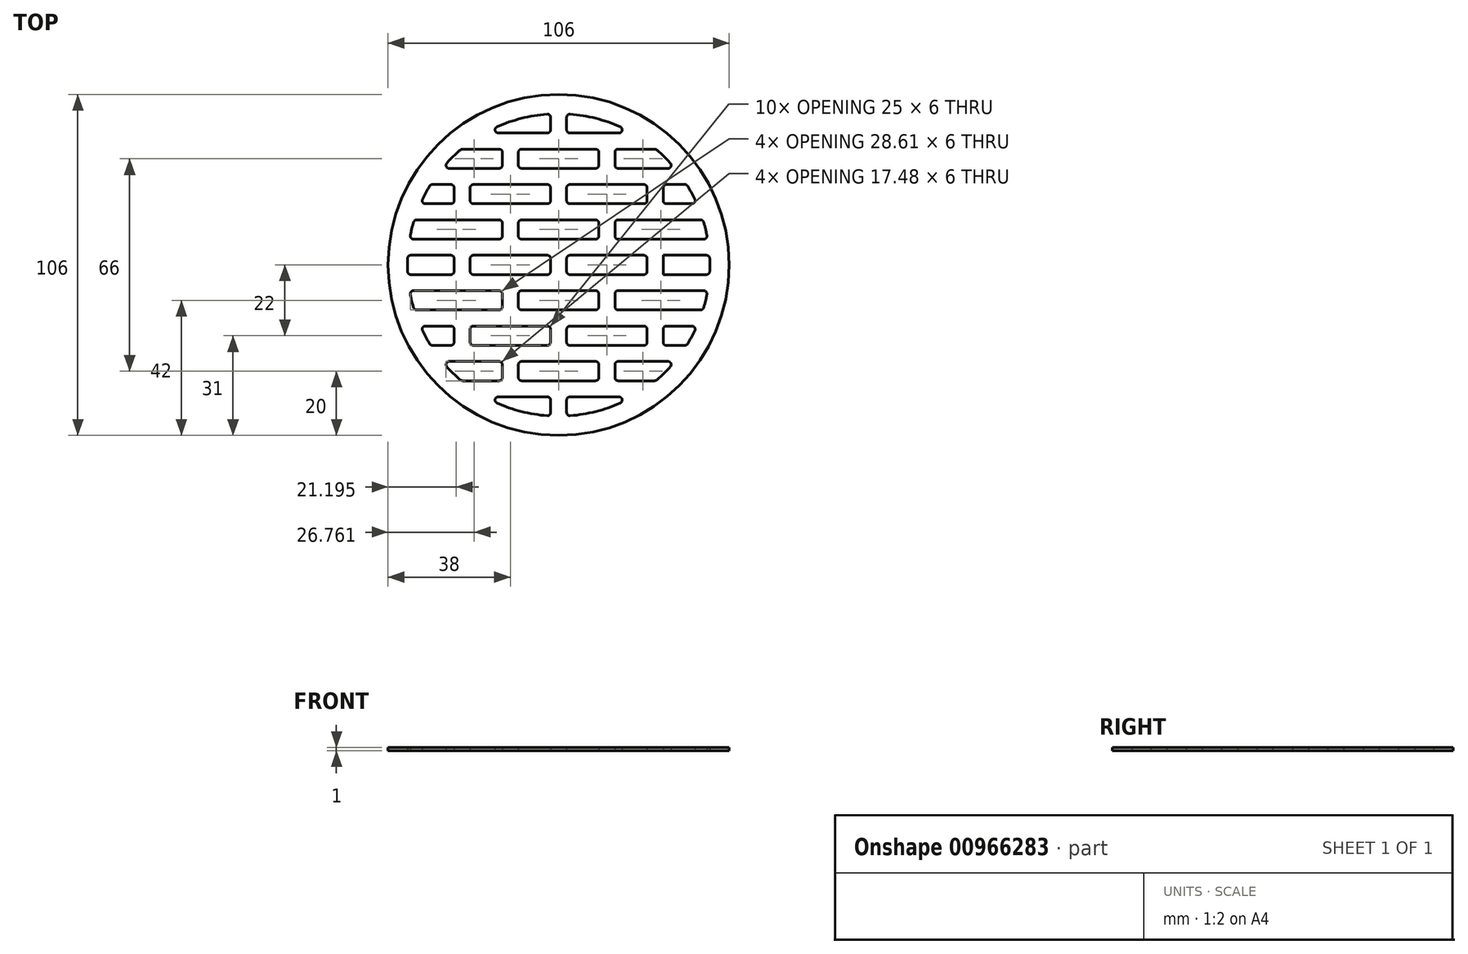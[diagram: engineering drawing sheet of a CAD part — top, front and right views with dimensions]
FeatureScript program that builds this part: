
annotation { "Feature Type Name" : "Feature", "Feature Type Description" : "" }
export const myFeature = defineFeature(function(context is Context, id is Id, definition is map)
    precondition{}
    {
        {
            var Q0;
            Q0=qCreatedBy(makeId("Top.planeOp"),FACE);
            var sketch = newSketch(context, id + "F0", { "sketchPlane" : qUnion([Q0])});
            skCircle(sketch, "E0", {"center": v(0, 0) * mm, "radius": 53 * mm});
            skArc(sketch, "E1", {"start": v(22.98, 41) * mm, "mid": v(13.08, 45.14) * mm, "end": v(2.5, 46.93) * mm});
            skLineSegment(sketch, "E2", {"start": v(-47, 0) * mm, "end": v(47, 0) * mm, "construction": true});
            skLineSegment(sketch, "E3.0", {"start": v(-46.9, -3) * mm, "end": v(-32.5, -3) * mm});
            skLineSegment(sketch, "E4.0", {"start": v(-46.9, 3) * mm, "end": v(-32.5, 3) * mm});
            skLineSegment(sketch, "E5", {"start": v(0, 47) * mm, "end": v(0, -47) * mm, "construction": true});
            skLineSegment(sketch, "E6.0", {"start": v(2.5, 46.93) * mm, "end": v(2.5, 41) * mm});
            skLineSegment(sketch, "E7.0", {"start": v(-2.5, 46.93) * mm, "end": v(-2.5, 41) * mm});
            skLineSegment(sketch, "E8.0.1.0", {"start": v(-46.9, 8) * mm, "end": v(-17.5, 8) * mm});
            skLineSegment(sketch, "E8.0.1.1", {"start": v(-44.87, 14) * mm, "end": v(-17.5, 14) * mm});
            skLineSegment(sketch, "E8.0.2.0", {"start": v(-42.99, 19) * mm, "end": v(-32.5, 19) * mm});
            skLineSegment(sketch, "E8.0.2.1", {"start": v(-39.8, 25) * mm, "end": v(-32.5, 25) * mm});
            skLineSegment(sketch, "E8.0.3.0", {"start": v(-36.18, 30) * mm, "end": v(-17.5, 30) * mm});
            skLineSegment(sketch, "E8.direction1", {"start": v(-46.9, -3) * mm, "end": v(-32.5, -3) * mm, "construction": true});
            skLineSegment(sketch, "E8.direction2", {"start": v(-46.9, -3) * mm, "end": v(-46.9, 8) * mm, "construction": true});
            skLineSegment(sketch, "E9.trimOffspring", {"start": v(-27.5, 3) * mm, "end": v(-27.5, -3) * mm});
            skLineSegment(sketch, "E10.trimOffspring", {"start": v(-32.5, 3) * mm, "end": v(-32.5, -3) * mm});
            skLineSegment(sketch, "E11.trimOffspring", {"start": v(-2.5, 3) * mm, "end": v(-2.5, -3) * mm});
            skLineSegment(sketch, "E12.trimOffspring", {"start": v(2.5, 3) * mm, "end": v(2.5, -3) * mm});
            skLineSegment(sketch, "E13.trimOffspring", {"start": v(-12.5, 14) * mm, "end": v(-12.5, 8) * mm});
            skLineSegment(sketch, "E14.trimOffspring", {"start": v(-17.5, 14) * mm, "end": v(-17.5, 8) * mm});
            skLineSegment(sketch, "E15.trimOffspring", {"start": v(2.5, 25) * mm, "end": v(2.5, 19) * mm});
            skLineSegment(sketch, "E16.trimOffspring", {"start": v(-2.5, 25) * mm, "end": v(-2.5, 19) * mm});
            skLineSegment(sketch, "E17.trimOffspring", {"start": v(-27.5, 25) * mm, "end": v(-27.5, 19) * mm});
            skLineSegment(sketch, "E18.trimOffspring", {"start": v(-32.5, 25) * mm, "end": v(-32.5, 19) * mm});
            skLineSegment(sketch, "E19.trimOffspring", {"start": v(-12.5, 36) * mm, "end": v(-12.5, 30) * mm});
            skLineSegment(sketch, "E20.trimOffspring", {"start": v(-17.5, 36) * mm, "end": v(-17.5, 30) * mm});
            skLineSegment(sketch, "E21.trimOffspring", {"start": v(-22.98, 41) * mm, "end": v(-2.5, 41) * mm});
            skLineSegment(sketch, "E22.trimOffspring", {"start": v(-30.22, 36) * mm, "end": v(-17.5, 36) * mm});
            skPoint(sketch, "E23.orphan", {"position": v(-46.9, 30) * mm});
            skPoint(sketch, "E24.orphan", {"position": v(-46.9, 25) * mm});
            skPoint(sketch, "E25.orphan", {"position": v(-46.9, 19) * mm});
            skPoint(sketch, "E26.orphan", {"position": v(-46.9, 14) * mm});
            skPoint(sketch, "E27.orphan", {"position": v(46.9, 8) * mm});
            skPoint(sketch, "E28.orphan", {"position": v(46.9, 14) * mm});
            skPoint(sketch, "E29.orphan", {"position": v(46.9, 19) * mm});
            skPoint(sketch, "E30.orphan", {"position": v(46.9, 25) * mm});
            skPoint(sketch, "E31.orphan", {"position": v(46.9, 30) * mm});
            skPoint(sketch, "E32.orphan", {"position": v(46.9, 41) * mm});
            skArc(sketch, "E33.trimOffspring", {"start": v(-30.22, 36) * mm, "mid": v(-33.33, 33.13) * mm, "end": v(-36.18, 30) * mm});
            skArc(sketch, "E34.trimOffspring", {"start": v(-39.8, 25) * mm, "mid": v(-41.5, 22.06) * mm, "end": v(-42.99, 19) * mm});
            skArc(sketch, "E35.trimOffspring", {"start": v(36.18, 30) * mm, "mid": v(33.33, 33.13) * mm, "end": v(30.22, 36) * mm});
            skArc(sketch, "E36.trimOffspring", {"start": v(42.99, 19) * mm, "mid": v(41.5, 22.06) * mm, "end": v(39.8, 25) * mm});
            skArc(sketch, "E37.trimOffspring", {"start": v(-44.87, 14) * mm, "mid": v(-45.69, 11.02) * mm, "end": v(-46.31, 8) * mm});
            skArc(sketch, "E38.trimOffspring", {"start": v(46.31, 8) * mm, "mid": v(45.69, 11.02) * mm, "end": v(44.87, 14) * mm});
            skArc(sketch, "E39.trimOffspring", {"start": v(-46.9, 3) * mm, "mid": v(-47, 0) * mm, "end": v(-46.9, -3) * mm});
            skLineSegment(sketch, "E40.MirrorCS", {"start": v(27.5, 3) * mm, "end": v(27.5, -3) * mm});
            skLineSegment(sketch, "E41.MirrorCS", {"start": v(32.5, 3) * mm, "end": v(32.5, -3) * mm});
            skLineSegment(sketch, "E42.MirrorCS", {"start": v(17.5, 14) * mm, "end": v(17.5, 8) * mm});
            skLineSegment(sketch, "E43.MirrorCS", {"start": v(12.5, 14) * mm, "end": v(12.5, 8) * mm});
            skLineSegment(sketch, "E44.MirrorCS", {"start": v(27.5, 25) * mm, "end": v(27.5, 19) * mm});
            skLineSegment(sketch, "E45.MirrorCS", {"start": v(32.5, 25) * mm, "end": v(32.5, 19) * mm});
            skLineSegment(sketch, "E46.MirrorCS", {"start": v(12.5, 36) * mm, "end": v(12.5, 30) * mm});
            skLineSegment(sketch, "E47.MirrorCS", {"start": v(17.5, 36) * mm, "end": v(17.5, 30) * mm});
            skLineSegment(sketch, "E48.MirrorCS", {"start": v(-12.5, -36) * mm, "end": v(-12.5, -30) * mm});
            skLineSegment(sketch, "E49.MirrorCS", {"start": v(12.5, -36) * mm, "end": v(12.5, -30) * mm});
            skArc(sketch, "E50.MirrorCS", {"start": v(46.31, -8) * mm, "mid": v(45.69, -11.02) * mm, "end": v(44.87, -14) * mm});
            skArc(sketch, "E51.MirrorCS", {"start": v(-44.87, -14) * mm, "mid": v(-45.69, -11.02) * mm, "end": v(-46.31, -8) * mm});
            skLineSegment(sketch, "E52.MirrorCS", {"start": v(-17.5, -36) * mm, "end": v(-17.5, -30) * mm});
            skLineSegment(sketch, "E53.MirrorCS", {"start": v(17.5, -36) * mm, "end": v(17.5, -30) * mm});
            skLineSegment(sketch, "E54.MirrorCS", {"start": v(-12.5, -14) * mm, "end": v(-12.5, -8) * mm});
            skPoint(sketch, "E55.MirrorP", {"position": v(-46.9, -25) * mm});
            skLineSegment(sketch, "E56.MirrorCS", {"start": v(2.5, -46.93) * mm, "end": v(2.5, -41) * mm});
            skLineSegment(sketch, "E57.MirrorCS", {"start": v(2.5, -25) * mm, "end": v(2.5, -19) * mm});
            skArc(sketch, "E58.MirrorCS", {"start": v(-30.22, -36) * mm, "mid": v(-33.33, -33.13) * mm, "end": v(-36.18, -30) * mm});
            skLineSegment(sketch, "E59.MirrorCS", {"start": v(12.5, -14) * mm, "end": v(12.5, -8) * mm});
            skArc(sketch, "E60.MirrorCS", {"start": v(42.99, -19) * mm, "mid": v(41.5, -22.06) * mm, "end": v(39.8, -25) * mm});
            skPoint(sketch, "E61.MirrorP", {"position": v(46.9, -14) * mm});
            skArc(sketch, "E62.MirrorCS", {"start": v(22.98, -41) * mm, "mid": v(13.08, -45.14) * mm, "end": v(2.5, -46.93) * mm});
            skLineSegment(sketch, "E63.MirrorCS", {"start": v(-44.87, -14) * mm, "end": v(-17.5, -14) * mm});
            skLineSegment(sketch, "E64.MirrorCS", {"start": v(-2.5, -25) * mm, "end": v(-2.5, -19) * mm});
            skLineSegment(sketch, "E65.MirrorCS", {"start": v(32.5, -25) * mm, "end": v(32.5, -19) * mm});
            skLineSegment(sketch, "E66.MirrorCS", {"start": v(17.5, -14) * mm, "end": v(17.5, -8) * mm});
            skPoint(sketch, "E67.MirrorP", {"position": v(-46.9, -30) * mm});
            skLineSegment(sketch, "E68.MirrorCS", {"start": v(-17.5, -14) * mm, "end": v(-17.5, -8) * mm});
            skArc(sketch, "E69.MirrorCS", {"start": v(36.18, -30) * mm, "mid": v(33.33, -33.13) * mm, "end": v(30.22, -36) * mm});
            skPoint(sketch, "E70.MirrorP", {"position": v(-46.9, -19) * mm});
            skLineSegment(sketch, "E71.MirrorCS", {"start": v(-2.5, -46.93) * mm, "end": v(-2.5, -41) * mm});
            skPoint(sketch, "E72.MirrorP", {"position": v(46.9, -41) * mm});
            skPoint(sketch, "E73.MirrorP", {"position": v(46.9, -8) * mm});
            skLineSegment(sketch, "E74.MirrorCS", {"start": v(-46.31, -8) * mm, "end": v(-17.5, -8) * mm});
            skArc(sketch, "E75.MirrorCS", {"start": v(-39.8, -25) * mm, "mid": v(-41.5, -22.06) * mm, "end": v(-42.99, -19) * mm});
            skLineSegment(sketch, "E76.MirrorCS", {"start": v(-32.5, -25) * mm, "end": v(-32.5, -19) * mm});
            skLineSegment(sketch, "E77.MirrorCS", {"start": v(-36.18, -30) * mm, "end": v(-17.5, -30) * mm});
            skPoint(sketch, "E78.MirrorP", {"position": v(-46.9, -14) * mm});
            skLineSegment(sketch, "E79.MirrorCS", {"start": v(-30.22, -36) * mm, "end": v(-17.5, -36) * mm});
            skPoint(sketch, "E80.MirrorP", {"position": v(46.9, -30) * mm});
            skLineSegment(sketch, "E81.MirrorCS", {"start": v(-22.98, -41) * mm, "end": v(-2.5, -41) * mm});
            skLineSegment(sketch, "E82.MirrorCS", {"start": v(-27.5, -25) * mm, "end": v(-27.5, -19) * mm});
            skPoint(sketch, "E83.MirrorP", {"position": v(46.9, -25) * mm});
            skLineSegment(sketch, "E84.MirrorCS", {"start": v(27.5, -25) * mm, "end": v(27.5, -19) * mm});
            skLineSegment(sketch, "E85.MirrorCS", {"start": v(-42.99, -19) * mm, "end": v(-32.5, -19) * mm});
            skLineSegment(sketch, "E86.MirrorCS", {"start": v(-39.8, -25) * mm, "end": v(-32.5, -25) * mm});
            skPoint(sketch, "E87.MirrorP", {"position": v(46.9, -19) * mm});
            skLineSegment(sketch, "E88.trimOffspring", {"start": v(17.5, 36) * mm, "end": v(30.22, 36) * mm});
            skLineSegment(sketch, "E89.trimOffspring", {"start": v(17.5, 30) * mm, "end": v(36.18, 30) * mm});
            skLineSegment(sketch, "E90.trimOffspring", {"start": v(-12.5, 36) * mm, "end": v(12.5, 36) * mm});
            skLineSegment(sketch, "E91.trimOffspring", {"start": v(-12.5, 30) * mm, "end": v(12.5, 30) * mm});
            skLineSegment(sketch, "E92.trimOffspring", {"start": v(-27.5, 25) * mm, "end": v(-2.5, 25) * mm});
            skLineSegment(sketch, "E93.trimOffspring", {"start": v(-27.5, 19) * mm, "end": v(-2.5, 19) * mm});
            skLineSegment(sketch, "E94.trimOffspring", {"start": v(2.5, 25) * mm, "end": v(27.5, 25) * mm});
            skLineSegment(sketch, "E95.trimOffspring", {"start": v(2.5, 19) * mm, "end": v(27.5, 19) * mm});
            skLineSegment(sketch, "E96.trimOffspring", {"start": v(32.5, 25) * mm, "end": v(39.8, 25) * mm});
            skLineSegment(sketch, "E97.trimOffspring", {"start": v(32.5, 19) * mm, "end": v(42.99, 19) * mm});
            skLineSegment(sketch, "E98.trimOffspring", {"start": v(17.5, 14) * mm, "end": v(44.87, 14) * mm});
            skLineSegment(sketch, "E99.trimOffspring", {"start": v(17.5, 8) * mm, "end": v(46.31, 8) * mm});
            skLineSegment(sketch, "E100.trimOffspring", {"start": v(-12.5, 14) * mm, "end": v(12.5, 14) * mm});
            skLineSegment(sketch, "E101.trimOffspring", {"start": v(-12.5, 8) * mm, "end": v(12.5, 8) * mm});
            skLineSegment(sketch, "E102.trimOffspring", {"start": v(-27.5, 3) * mm, "end": v(-2.5, 3) * mm});
            skLineSegment(sketch, "E103.trimOffspring", {"start": v(-27.5, -3) * mm, "end": v(-25.91, -3) * mm, "construction": true});
            skLineSegment(sketch, "E104.trimOffspring", {"start": v(-27.5, -3) * mm, "end": v(-2.5, -3) * mm});
            skLineSegment(sketch, "E105.trimOffspring", {"start": v(2.5, 3) * mm, "end": v(27.5, 3) * mm});
            skLineSegment(sketch, "E106.trimOffspring", {"start": v(2.5, -3) * mm, "end": v(27.5, -3) * mm});
            skLineSegment(sketch, "E107.trimOffspring", {"start": v(32.5, -3) * mm, "end": v(46.9, -3) * mm});
            skLineSegment(sketch, "E108.trimOffspring", {"start": v(32.5, 3) * mm, "end": v(46.9, 3) * mm});
            skLineSegment(sketch, "E109.trimOffspring", {"start": v(17.5, -8) * mm, "end": v(46.31, -8) * mm});
            skLineSegment(sketch, "E110.trimOffspring", {"start": v(17.5, -14) * mm, "end": v(44.87, -14) * mm});
            skLineSegment(sketch, "E111.trimOffspring", {"start": v(-12.5, -8) * mm, "end": v(12.5, -8) * mm});
            skLineSegment(sketch, "E112.trimOffspring", {"start": v(-12.5, -14) * mm, "end": v(12.5, -14) * mm});
            skLineSegment(sketch, "E113.trimOffspring", {"start": v(-27.5, -19) * mm, "end": v(-2.5, -19) * mm});
            skLineSegment(sketch, "E114.trimOffspring", {"start": v(-27.5, -25) * mm, "end": v(-2.5, -25) * mm});
            skLineSegment(sketch, "E115.trimOffspring", {"start": v(2.5, -19) * mm, "end": v(27.5, -19) * mm});
            skLineSegment(sketch, "E116.trimOffspring", {"start": v(2.5, -25) * mm, "end": v(27.5, -25) * mm});
            skLineSegment(sketch, "E117.trimOffspring", {"start": v(32.5, -25) * mm, "end": v(39.8, -25) * mm});
            skLineSegment(sketch, "E118.trimOffspring", {"start": v(32.5, -19) * mm, "end": v(42.99, -19) * mm});
            skLineSegment(sketch, "E119.trimOffspring", {"start": v(17.5, -30) * mm, "end": v(36.18, -30) * mm});
            skLineSegment(sketch, "E120.trimOffspring", {"start": v(17.5, -36) * mm, "end": v(30.22, -36) * mm});
            skLineSegment(sketch, "E121.trimOffspring", {"start": v(-12.5, -30) * mm, "end": v(12.5, -30) * mm});
            skLineSegment(sketch, "E122.trimOffspring", {"start": v(-12.5, -36) * mm, "end": v(12.5, -36) * mm});
            skLineSegment(sketch, "E123.trimOffspring", {"start": v(2.5, -41) * mm, "end": v(22.98, -41) * mm});
            skArc(sketch, "E124.trimOffspring", {"start": v(2.5, -46.93) * mm, "mid": v(13.08, -45.14) * mm, "end": v(22.98, -41) * mm});
            skArc(sketch, "E125.trimOffspring", {"start": v(-2.5, -46.93) * mm, "mid": v(-13.08, -45.14) * mm, "end": v(-22.98, -41) * mm});
            skArc(sketch, "E126.trimOffspring", {"start": v(-2.5, 46.93) * mm, "mid": v(-13.08, 45.14) * mm, "end": v(-22.98, 41) * mm});
            skLineSegment(sketch, "E127.trimOffspring", {"start": v(2.5, 41) * mm, "end": v(22.98, 41) * mm});
            skArc(sketch, "E128.trimOffspring", {"start": v(46.9, -3) * mm, "mid": v(47, 0) * mm, "end": v(46.9, 3) * mm});
            skArc(sketch, "E129.trimOffspring", {"start": v(44.87, -14) * mm, "mid": v(45.69, -11.02) * mm, "end": v(46.31, -8) * mm});
            skArc(sketch, "E130.trimOffspring", {"start": v(39.8, -25) * mm, "mid": v(41.5, -22.06) * mm, "end": v(42.99, -19) * mm});
            skArc(sketch, "E131.trimOffspring", {"start": v(30.22, -36) * mm, "mid": v(33.33, -33.13) * mm, "end": v(36.18, -30) * mm});
            skArc(sketch, "E132.trimOffspring", {"start": v(-22.98, -41) * mm, "mid": v(-13.08, -45.14) * mm, "end": v(-2.5, -46.93) * mm});
            skArc(sketch, "E133.trimOffspring", {"start": v(-36.18, -30) * mm, "mid": v(-33.33, -33.13) * mm, "end": v(-30.22, -36) * mm});
            skArc(sketch, "E134.trimOffspring", {"start": v(-42.99, -19) * mm, "mid": v(-41.5, -22.06) * mm, "end": v(-39.8, -25) * mm});
            skArc(sketch, "E135.trimOffspring", {"start": v(-46.31, -8) * mm, "mid": v(-45.69, -11.02) * mm, "end": v(-44.87, -14) * mm});
            skPoint(sketch, "E136.orphan", {"position": v(-46.9, -8) * mm});
            skSolve(sketch);
        }
        {
            var Q0;
            Q0=qSketchRegion(id+"F0",true);
            extrude(context, id + "F1", {"entities" : qUnion([Q0]), "depth" : 1 * mm, "offsetDistance" : 25 * mm});
        }
        {
            var Q0;
            Q0=makeQuery(id+"F1.opExtrude","SWEPT_EDGE",EDGE,{"disambiguationData":[OSD([sQuery(id+"F0.wireOp",EDGE,"E1"),sQuery(id+"F0.wireOp",EDGE,"E127.trimOffspring")])]});
            var Q1;
            Q1=makeQuery(id+"F1.opExtrude","SWEPT_EDGE",EDGE,{"disambiguationData":[OSD([sQuery(id+"F0.wireOp",EDGE,"E21.trimOffspring"),sQuery(id+"F0.wireOp",EDGE,"E126.trimOffspring")])]});
            var Q2;
            Q2=makeQuery(id+"F1.opExtrude","SWEPT_EDGE",EDGE,{"disambiguationData":[OSD([sQuery(id+"F0.wireOp",EDGE,"E35.trimOffspring"),sQuery(id+"F0.wireOp",EDGE,"E89.trimOffspring")])]});
            var Q3;
            Q3=makeQuery(id+"F1.opExtrude","SWEPT_EDGE",EDGE,{"disambiguationData":[OSD([sQuery(id+"F0.wireOp",EDGE,"E36.trimOffspring"),sQuery(id+"F0.wireOp",EDGE,"E97.trimOffspring")])]});
            var Q4;
            Q4=makeQuery(id+"F1.opExtrude","SWEPT_EDGE",EDGE,{"disambiguationData":[OSD([sQuery(id+"F0.wireOp",EDGE,"E38.trimOffspring"),sQuery(id+"F0.wireOp",EDGE,"E99.trimOffspring")])]});
            var Q5;
            Q5=makeQuery(id+"F1.opExtrude","SWEPT_EDGE",EDGE,{"disambiguationData":[OSD([sQuery(id+"F0.wireOp",EDGE,"E109.trimOffspring"),sQuery(id+"F0.wireOp",EDGE,"E129.trimOffspring")])]});
            var Q6;
            Q6=makeQuery(id+"F1.opExtrude","SWEPT_EDGE",EDGE,{"disambiguationData":[OSD([sQuery(id+"F0.wireOp",EDGE,"E108.trimOffspring"),sQuery(id+"F0.wireOp",EDGE,"E128.trimOffspring")])]});
            var Q7;
            Q7=makeQuery(id+"F1.opExtrude","SWEPT_EDGE",EDGE,{"disambiguationData":[OSD([sQuery(id+"F0.wireOp",EDGE,"E107.trimOffspring"),sQuery(id+"F0.wireOp",EDGE,"E128.trimOffspring")])]});
            var Q8;
            Q8=makeQuery(id+"F1.opExtrude","SWEPT_EDGE",EDGE,{"disambiguationData":[OSD([sQuery(id+"F0.wireOp",EDGE,"E110.trimOffspring"),sQuery(id+"F0.wireOp",EDGE,"E129.trimOffspring")])]});
            var Q9;
            Q9=makeQuery(id+"F1.opExtrude","SWEPT_EDGE",EDGE,{"disambiguationData":[OSD([sQuery(id+"F0.wireOp",EDGE,"E117.trimOffspring"),sQuery(id+"F0.wireOp",EDGE,"E130.trimOffspring")])]});
            var Q10;
            Q10=makeQuery(id+"F1.opExtrude","SWEPT_EDGE",EDGE,{"disambiguationData":[OSD([sQuery(id+"F0.wireOp",EDGE,"E120.trimOffspring"),sQuery(id+"F0.wireOp",EDGE,"E131.trimOffspring")])]});
            var Q11;
            Q11=makeQuery(id+"F1.opExtrude","SWEPT_EDGE",EDGE,{"disambiguationData":[OSD([sQuery(id+"F0.wireOp",EDGE,"E123.trimOffspring"),sQuery(id+"F0.wireOp",EDGE,"E124.trimOffspring")])]});
            var Q12;
            Q12=makeQuery(id+"F1.opExtrude","SWEPT_EDGE",EDGE,{"disambiguationData":[OSD([sQuery(id+"F0.wireOp",EDGE,"E119.trimOffspring"),sQuery(id+"F0.wireOp",EDGE,"E131.trimOffspring")])]});
            var Q13;
            Q13=makeQuery(id+"F1.opExtrude","SWEPT_EDGE",EDGE,{"disambiguationData":[OSD([sQuery(id+"F0.wireOp",EDGE,"E118.trimOffspring"),sQuery(id+"F0.wireOp",EDGE,"E130.trimOffspring")])]});
            var Q14;
            Q14=makeQuery(id+"F1.opExtrude","SWEPT_EDGE",EDGE,{"disambiguationData":[OSD([sQuery(id+"F0.wireOp",EDGE,"E38.trimOffspring"),sQuery(id+"F0.wireOp",EDGE,"E98.trimOffspring")])]});
            var Q15;
            Q15=makeQuery(id+"F1.opExtrude","SWEPT_EDGE",EDGE,{"disambiguationData":[OSD([sQuery(id+"F0.wireOp",EDGE,"E36.trimOffspring"),sQuery(id+"F0.wireOp",EDGE,"E96.trimOffspring")])]});
            var Q16;
            Q16=makeQuery(id+"F1.opExtrude","SWEPT_EDGE",EDGE,{"disambiguationData":[OSD([sQuery(id+"F0.wireOp",EDGE,"E35.trimOffspring"),sQuery(id+"F0.wireOp",EDGE,"E88.trimOffspring")])]});
            var Q17;
            Q17=makeQuery(id+"F1.opExtrude","SWEPT_EDGE",EDGE,{"disambiguationData":[OSD([sQuery(id+"F0.wireOp",EDGE,"E7.0"),sQuery(id+"F0.wireOp",EDGE,"E126.trimOffspring")])]});
            var Q18;
            Q18=makeQuery(id+"F1.opExtrude","SWEPT_EDGE",EDGE,{"disambiguationData":[OSD([sQuery(id+"F0.wireOp",EDGE,"E7.0"),sQuery(id+"F0.wireOp",EDGE,"E21.trimOffspring")])]});
            var Q19;
            Q19=makeQuery(id+"F1.opExtrude","SWEPT_EDGE",EDGE,{"disambiguationData":[OSD([sQuery(id+"F0.wireOp",EDGE,"E1"),sQuery(id+"F0.wireOp",EDGE,"E6.0")])]});
            var Q20;
            Q20=makeQuery(id+"F1.opExtrude","SWEPT_EDGE",EDGE,{"disambiguationData":[OSD([sQuery(id+"F0.wireOp",EDGE,"E6.0"),sQuery(id+"F0.wireOp",EDGE,"E127.trimOffspring")])]});
            var Q21;
            Q21=makeQuery(id+"F1.opExtrude","SWEPT_EDGE",EDGE,{"disambiguationData":[OSD([sQuery(id+"F0.wireOp",EDGE,"E8.0.3.0"),sQuery(id+"F0.wireOp",EDGE,"E33.trimOffspring")])]});
            var Q22;
            Q22=makeQuery(id+"F1.opExtrude","SWEPT_EDGE",EDGE,{"disambiguationData":[OSD([sQuery(id+"F0.wireOp",EDGE,"E22.trimOffspring"),sQuery(id+"F0.wireOp",EDGE,"E33.trimOffspring")])]});
            var Q23;
            Q23=makeQuery(id+"F1.opExtrude","SWEPT_EDGE",EDGE,{"disambiguationData":[OSD([sQuery(id+"F0.wireOp",EDGE,"E20.trimOffspring"),sQuery(id+"F0.wireOp",EDGE,"E22.trimOffspring")])]});
            var Q24;
            Q24=makeQuery(id+"F1.opExtrude","SWEPT_EDGE",EDGE,{"disambiguationData":[OSD([sQuery(id+"F0.wireOp",EDGE,"E8.0.3.0"),sQuery(id+"F0.wireOp",EDGE,"E20.trimOffspring")])]});
            var Q25;
            Q25=makeQuery(id+"F1.opExtrude","SWEPT_EDGE",EDGE,{"disambiguationData":[OSD([sQuery(id+"F0.wireOp",EDGE,"E16.trimOffspring"),sQuery(id+"F0.wireOp",EDGE,"E93.trimOffspring")])]});
            var Q26;
            Q26=makeQuery(id+"F1.opExtrude","SWEPT_EDGE",EDGE,{"disambiguationData":[OSD([sQuery(id+"F0.wireOp",EDGE,"E8.0.2.0"),sQuery(id+"F0.wireOp",EDGE,"E18.trimOffspring")])]});
            var Q27;
            Q27=makeQuery(id+"F1.opExtrude","SWEPT_EDGE",EDGE,{"disambiguationData":[OSD([sQuery(id+"F0.wireOp",EDGE,"E8.0.2.1"),sQuery(id+"F0.wireOp",EDGE,"E18.trimOffspring")])]});
            var Q28;
            Q28=makeQuery(id+"F1.opExtrude","SWEPT_EDGE",EDGE,{"disambiguationData":[OSD([sQuery(id+"F0.wireOp",EDGE,"E8.0.2.1"),sQuery(id+"F0.wireOp",EDGE,"E34.trimOffspring")])]});
            var Q29;
            Q29=makeQuery(id+"F1.opExtrude","SWEPT_EDGE",EDGE,{"disambiguationData":[OSD([sQuery(id+"F0.wireOp",EDGE,"E8.0.2.0"),sQuery(id+"F0.wireOp",EDGE,"E34.trimOffspring")])]});
            var Q30;
            Q30=makeQuery(id+"F1.opExtrude","SWEPT_EDGE",EDGE,{"disambiguationData":[OSD([sQuery(id+"F0.wireOp",EDGE,"E17.trimOffspring"),sQuery(id+"F0.wireOp",EDGE,"E93.trimOffspring")])]});
            var Q31;
            Q31=makeQuery(id+"F1.opExtrude","SWEPT_EDGE",EDGE,{"disambiguationData":[OSD([sQuery(id+"F0.wireOp",EDGE,"E17.trimOffspring"),sQuery(id+"F0.wireOp",EDGE,"E92.trimOffspring")])]});
            var Q32;
            Q32=makeQuery(id+"F1.opExtrude","SWEPT_EDGE",EDGE,{"disambiguationData":[OSD([sQuery(id+"F0.wireOp",EDGE,"E16.trimOffspring"),sQuery(id+"F0.wireOp",EDGE,"E92.trimOffspring")])]});
            var Q33;
            Q33=makeQuery(id+"F1.opExtrude","SWEPT_EDGE",EDGE,{"disambiguationData":[OSD([sQuery(id+"F0.wireOp",EDGE,"E46.MirrorCS"),sQuery(id+"F0.wireOp",EDGE,"E90.trimOffspring")])]});
            var Q34;
            Q34=makeQuery(id+"F1.opExtrude","SWEPT_EDGE",EDGE,{"disambiguationData":[OSD([sQuery(id+"F0.wireOp",EDGE,"E19.trimOffspring"),sQuery(id+"F0.wireOp",EDGE,"E90.trimOffspring")])]});
            var Q35;
            Q35=makeQuery(id+"F1.opExtrude","SWEPT_EDGE",EDGE,{"disambiguationData":[OSD([sQuery(id+"F0.wireOp",EDGE,"E19.trimOffspring"),sQuery(id+"F0.wireOp",EDGE,"E91.trimOffspring")])]});
            var Q36;
            Q36=makeQuery(id+"F1.opExtrude","SWEPT_EDGE",EDGE,{"disambiguationData":[OSD([sQuery(id+"F0.wireOp",EDGE,"E46.MirrorCS"),sQuery(id+"F0.wireOp",EDGE,"E91.trimOffspring")])]});
            var Q37;
            Q37=makeQuery(id+"F1.opExtrude","SWEPT_EDGE",EDGE,{"disambiguationData":[OSD([sQuery(id+"F0.wireOp",EDGE,"E47.MirrorCS"),sQuery(id+"F0.wireOp",EDGE,"E89.trimOffspring")])]});
            var Q38;
            Q38=makeQuery(id+"F1.opExtrude","SWEPT_EDGE",EDGE,{"disambiguationData":[OSD([sQuery(id+"F0.wireOp",EDGE,"E47.MirrorCS"),sQuery(id+"F0.wireOp",EDGE,"E88.trimOffspring")])]});
            var Q39;
            Q39=makeQuery(id+"F1.opExtrude","SWEPT_EDGE",EDGE,{"disambiguationData":[OSD([sQuery(id+"F0.wireOp",EDGE,"E45.MirrorCS"),sQuery(id+"F0.wireOp",EDGE,"E96.trimOffspring")])]});
            var Q40;
            Q40=makeQuery(id+"F1.opExtrude","SWEPT_EDGE",EDGE,{"disambiguationData":[OSD([sQuery(id+"F0.wireOp",EDGE,"E45.MirrorCS"),sQuery(id+"F0.wireOp",EDGE,"E97.trimOffspring")])]});
            var Q41;
            Q41=makeQuery(id+"F1.opExtrude","SWEPT_EDGE",EDGE,{"disambiguationData":[OSD([sQuery(id+"F0.wireOp",EDGE,"E44.MirrorCS"),sQuery(id+"F0.wireOp",EDGE,"E95.trimOffspring")])]});
            var Q42;
            Q42=makeQuery(id+"F1.opExtrude","SWEPT_EDGE",EDGE,{"disambiguationData":[OSD([sQuery(id+"F0.wireOp",EDGE,"E44.MirrorCS"),sQuery(id+"F0.wireOp",EDGE,"E94.trimOffspring")])]});
            var Q43;
            Q43=makeQuery(id+"F1.opExtrude","SWEPT_EDGE",EDGE,{"disambiguationData":[OSD([sQuery(id+"F0.wireOp",EDGE,"E15.trimOffspring"),sQuery(id+"F0.wireOp",EDGE,"E94.trimOffspring")])]});
            var Q44;
            Q44=makeQuery(id+"F1.opExtrude","SWEPT_EDGE",EDGE,{"disambiguationData":[OSD([sQuery(id+"F0.wireOp",EDGE,"E15.trimOffspring"),sQuery(id+"F0.wireOp",EDGE,"E95.trimOffspring")])]});
            var Q45;
            Q45=makeQuery(id+"F1.opExtrude","SWEPT_EDGE",EDGE,{"disambiguationData":[OSD([sQuery(id+"F0.wireOp",EDGE,"E42.MirrorCS"),sQuery(id+"F0.wireOp",EDGE,"E98.trimOffspring")])]});
            var Q46;
            Q46=makeQuery(id+"F1.opExtrude","SWEPT_EDGE",EDGE,{"disambiguationData":[OSD([sQuery(id+"F0.wireOp",EDGE,"E42.MirrorCS"),sQuery(id+"F0.wireOp",EDGE,"E99.trimOffspring")])]});
            var Q47;
            Q47=makeQuery(id+"F1.opExtrude","SWEPT_EDGE",EDGE,{"disambiguationData":[OSD([sQuery(id+"F0.wireOp",EDGE,"E13.trimOffspring"),sQuery(id+"F0.wireOp",EDGE,"E101.trimOffspring")])]});
            var Q48;
            Q48=makeQuery(id+"F1.opExtrude","SWEPT_EDGE",EDGE,{"disambiguationData":[OSD([sQuery(id+"F0.wireOp",EDGE,"E8.0.1.0"),sQuery(id+"F0.wireOp",EDGE,"E37.trimOffspring")])]});
            var Q49;
            Q49=makeQuery(id+"F1.opExtrude","SWEPT_EDGE",EDGE,{"disambiguationData":[OSD([sQuery(id+"F0.wireOp",EDGE,"E13.trimOffspring"),sQuery(id+"F0.wireOp",EDGE,"E100.trimOffspring")])]});
            var Q50;
            Q50=makeQuery(id+"F1.opExtrude","SWEPT_EDGE",EDGE,{"disambiguationData":[OSD([sQuery(id+"F0.wireOp",EDGE,"E8.0.1.1"),sQuery(id+"F0.wireOp",EDGE,"E37.trimOffspring")])]});
            var Q51;
            Q51=makeQuery(id+"F1.opExtrude","SWEPT_EDGE",EDGE,{"disambiguationData":[OSD([sQuery(id+"F0.wireOp",EDGE,"E8.0.1.1"),sQuery(id+"F0.wireOp",EDGE,"E14.trimOffspring")])]});
            var Q52;
            Q52=makeQuery(id+"F1.opExtrude","SWEPT_EDGE",EDGE,{"disambiguationData":[OSD([sQuery(id+"F0.wireOp",EDGE,"E8.0.1.0"),sQuery(id+"F0.wireOp",EDGE,"E14.trimOffspring")])]});
            var Q53;
            Q53=makeQuery(id+"F1.opExtrude","SWEPT_EDGE",EDGE,{"disambiguationData":[OSD([sQuery(id+"F0.wireOp",EDGE,"E43.MirrorCS"),sQuery(id+"F0.wireOp",EDGE,"E101.trimOffspring")])]});
            var Q54;
            Q54=makeQuery(id+"F1.opExtrude","SWEPT_EDGE",EDGE,{"disambiguationData":[OSD([sQuery(id+"F0.wireOp",EDGE,"E43.MirrorCS"),sQuery(id+"F0.wireOp",EDGE,"E100.trimOffspring")])]});
            var Q55;
            Q55=makeQuery(id+"F1.opExtrude","SWEPT_EDGE",EDGE,{"disambiguationData":[OSD([sQuery(id+"F0.wireOp",EDGE,"E40.MirrorCS"),sQuery(id+"F0.wireOp",EDGE,"E105.trimOffspring")])]});
            var Q56;
            Q56=makeQuery(id+"F1.opExtrude","SWEPT_EDGE",EDGE,{"disambiguationData":[OSD([sQuery(id+"F0.wireOp",EDGE,"E40.MirrorCS"),sQuery(id+"F0.wireOp",EDGE,"E106.trimOffspring")])]});
            var Q57;
            Q57=makeQuery(id+"F1.opExtrude","SWEPT_EDGE",EDGE,{"disambiguationData":[OSD([sQuery(id+"F0.wireOp",EDGE,"E11.trimOffspring"),sQuery(id+"F0.wireOp",EDGE,"E104.trimOffspring")])]});
            var Q58;
            Q58=makeQuery(id+"F1.opExtrude","SWEPT_EDGE",EDGE,{"disambiguationData":[OSD([sQuery(id+"F0.wireOp",EDGE,"E11.trimOffspring"),sQuery(id+"F0.wireOp",EDGE,"E102.trimOffspring")])]});
            var Q59;
            Q59=makeQuery(id+"F1.opExtrude","SWEPT_EDGE",EDGE,{"disambiguationData":[OSD([sQuery(id+"F0.wireOp",EDGE,"E4.0"),sQuery(id+"F0.wireOp",EDGE,"E10.trimOffspring")])]});
            var Q60;
            Q60=makeQuery(id+"F1.opExtrude","SWEPT_EDGE",EDGE,{"disambiguationData":[OSD([sQuery(id+"F0.wireOp",EDGE,"E3.0"),sQuery(id+"F0.wireOp",EDGE,"E10.trimOffspring")])]});
            var Q61;
            Q61=makeQuery(id+"F1.opExtrude","SWEPT_EDGE",EDGE,{"disambiguationData":[OSD([sQuery(id+"F0.wireOp",EDGE,"E4.0"),sQuery(id+"F0.wireOp",EDGE,"E39.trimOffspring")])]});
            var Q62;
            Q62=makeQuery(id+"F1.opExtrude","SWEPT_EDGE",EDGE,{"disambiguationData":[OSD([sQuery(id+"F0.wireOp",EDGE,"E63.MirrorCS"),sQuery(id+"F0.wireOp",EDGE,"E135.trimOffspring")])]});
            var Q63;
            Q63=makeQuery(id+"F1.opExtrude","SWEPT_EDGE",EDGE,{"disambiguationData":[OSD([sQuery(id+"F0.wireOp",EDGE,"E3.0"),sQuery(id+"F0.wireOp",EDGE,"E39.trimOffspring")])]});
            var Q64;
            Q64=makeQuery(id+"F1.opExtrude","SWEPT_EDGE",EDGE,{"disambiguationData":[OSD([sQuery(id+"F0.wireOp",EDGE,"E9.trimOffspring"),sQuery(id+"F0.wireOp",EDGE,"E104.trimOffspring")])]});
            var Q65;
            Q65=makeQuery(id+"F1.opExtrude","SWEPT_EDGE",EDGE,{"disambiguationData":[OSD([sQuery(id+"F0.wireOp",EDGE,"E12.trimOffspring"),sQuery(id+"F0.wireOp",EDGE,"E106.trimOffspring")])]});
            var Q66;
            Q66=makeQuery(id+"F1.opExtrude","SWEPT_EDGE",EDGE,{"disambiguationData":[OSD([sQuery(id+"F0.wireOp",EDGE,"E12.trimOffspring"),sQuery(id+"F0.wireOp",EDGE,"E105.trimOffspring")])]});
            var Q67;
            Q67=makeQuery(id+"F1.opExtrude","SWEPT_EDGE",EDGE,{"disambiguationData":[OSD([sQuery(id+"F0.wireOp",EDGE,"E68.MirrorCS"),sQuery(id+"F0.wireOp",EDGE,"E74.MirrorCS")])]});
            var Q68;
            Q68=makeQuery(id+"F1.opExtrude","SWEPT_EDGE",EDGE,{"disambiguationData":[OSD([sQuery(id+"F0.wireOp",EDGE,"E63.MirrorCS"),sQuery(id+"F0.wireOp",EDGE,"E68.MirrorCS")])]});
            var Q69;
            Q69=makeQuery(id+"F1.opExtrude","SWEPT_EDGE",EDGE,{"disambiguationData":[OSD([sQuery(id+"F0.wireOp",EDGE,"E74.MirrorCS"),sQuery(id+"F0.wireOp",EDGE,"E135.trimOffspring")])]});
            var Q70;
            Q70=makeQuery(id+"F1.opExtrude","SWEPT_EDGE",EDGE,{"disambiguationData":[OSD([sQuery(id+"F0.wireOp",EDGE,"E54.MirrorCS"),sQuery(id+"F0.wireOp",EDGE,"E111.trimOffspring")])]});
            var Q71;
            Q71=makeQuery(id+"F1.opExtrude","SWEPT_EDGE",EDGE,{"disambiguationData":[OSD([sQuery(id+"F0.wireOp",EDGE,"E54.MirrorCS"),sQuery(id+"F0.wireOp",EDGE,"E112.trimOffspring")])]});
            var Q72;
            Q72=makeQuery(id+"F1.opExtrude","SWEPT_EDGE",EDGE,{"disambiguationData":[OSD([sQuery(id+"F0.wireOp",EDGE,"E59.MirrorCS"),sQuery(id+"F0.wireOp",EDGE,"E112.trimOffspring")])]});
            var Q73;
            Q73=makeQuery(id+"F1.opExtrude","SWEPT_EDGE",EDGE,{"disambiguationData":[OSD([sQuery(id+"F0.wireOp",EDGE,"E59.MirrorCS"),sQuery(id+"F0.wireOp",EDGE,"E111.trimOffspring")])]});
            var Q74;
            Q74=makeQuery(id+"F1.opExtrude","SWEPT_EDGE",EDGE,{"disambiguationData":[OSD([sQuery(id+"F0.wireOp",EDGE,"E66.MirrorCS"),sQuery(id+"F0.wireOp",EDGE,"E109.trimOffspring")])]});
            var Q75;
            Q75=makeQuery(id+"F1.opExtrude","SWEPT_EDGE",EDGE,{"disambiguationData":[OSD([sQuery(id+"F0.wireOp",EDGE,"E66.MirrorCS"),sQuery(id+"F0.wireOp",EDGE,"E110.trimOffspring")])]});
            var Q76;
            Q76=makeQuery(id+"F1.opExtrude","SWEPT_EDGE",EDGE,{"disambiguationData":[OSD([sQuery(id+"F0.wireOp",EDGE,"E65.MirrorCS"),sQuery(id+"F0.wireOp",EDGE,"E118.trimOffspring")])]});
            var Q77;
            Q77=makeQuery(id+"F1.opExtrude","SWEPT_EDGE",EDGE,{"disambiguationData":[OSD([sQuery(id+"F0.wireOp",EDGE,"E65.MirrorCS"),sQuery(id+"F0.wireOp",EDGE,"E117.trimOffspring")])]});
            var Q78;
            Q78=makeQuery(id+"F1.opExtrude","SWEPT_EDGE",EDGE,{"disambiguationData":[OSD([sQuery(id+"F0.wireOp",EDGE,"E53.MirrorCS"),sQuery(id+"F0.wireOp",EDGE,"E120.trimOffspring")])]});
            var Q79;
            Q79=makeQuery(id+"F1.opExtrude","SWEPT_EDGE",EDGE,{"disambiguationData":[OSD([sQuery(id+"F0.wireOp",EDGE,"E53.MirrorCS"),sQuery(id+"F0.wireOp",EDGE,"E119.trimOffspring")])]});
            var Q80;
            Q80=makeQuery(id+"F1.opExtrude","SWEPT_EDGE",EDGE,{"disambiguationData":[OSD([sQuery(id+"F0.wireOp",EDGE,"E57.MirrorCS"),sQuery(id+"F0.wireOp",EDGE,"E115.trimOffspring")])]});
            var Q81;
            Q81=makeQuery(id+"F1.opExtrude","SWEPT_EDGE",EDGE,{"disambiguationData":[OSD([sQuery(id+"F0.wireOp",EDGE,"E84.MirrorCS"),sQuery(id+"F0.wireOp",EDGE,"E115.trimOffspring")])]});
            var Q82;
            Q82=makeQuery(id+"F1.opExtrude","SWEPT_EDGE",EDGE,{"disambiguationData":[OSD([sQuery(id+"F0.wireOp",EDGE,"E84.MirrorCS"),sQuery(id+"F0.wireOp",EDGE,"E116.trimOffspring")])]});
            var Q83;
            Q83=makeQuery(id+"F1.opExtrude","SWEPT_EDGE",EDGE,{"disambiguationData":[OSD([sQuery(id+"F0.wireOp",EDGE,"E57.MirrorCS"),sQuery(id+"F0.wireOp",EDGE,"E116.trimOffspring")])]});
            var Q84;
            Q84=makeQuery(id+"F1.opExtrude","SWEPT_EDGE",EDGE,{"disambiguationData":[OSD([sQuery(id+"F0.wireOp",EDGE,"E48.MirrorCS"),sQuery(id+"F0.wireOp",EDGE,"E122.trimOffspring")])]});
            var Q85;
            Q85=makeQuery(id+"F1.opExtrude","SWEPT_EDGE",EDGE,{"disambiguationData":[OSD([sQuery(id+"F0.wireOp",EDGE,"E79.MirrorCS"),sQuery(id+"F0.wireOp",EDGE,"E133.trimOffspring")])]});
            var Q86;
            Q86=makeQuery(id+"F1.opExtrude","SWEPT_EDGE",EDGE,{"disambiguationData":[OSD([sQuery(id+"F0.wireOp",EDGE,"E77.MirrorCS"),sQuery(id+"F0.wireOp",EDGE,"E133.trimOffspring")])]});
            var Q87;
            Q87=makeQuery(id+"F1.opExtrude","SWEPT_EDGE",EDGE,{"disambiguationData":[OSD([sQuery(id+"F0.wireOp",EDGE,"E52.MirrorCS"),sQuery(id+"F0.wireOp",EDGE,"E77.MirrorCS")])]});
            var Q88;
            Q88=makeQuery(id+"F1.opExtrude","SWEPT_EDGE",EDGE,{"disambiguationData":[OSD([sQuery(id+"F0.wireOp",EDGE,"E52.MirrorCS"),sQuery(id+"F0.wireOp",EDGE,"E79.MirrorCS")])]});
            var Q89;
            Q89=makeQuery(id+"F1.opExtrude","SWEPT_EDGE",EDGE,{"disambiguationData":[OSD([sQuery(id+"F0.wireOp",EDGE,"E71.MirrorCS"),sQuery(id+"F0.wireOp",EDGE,"E132.trimOffspring")])]});
            var Q90;
            Q90=makeQuery(id+"F1.opExtrude","SWEPT_EDGE",EDGE,{"disambiguationData":[OSD([sQuery(id+"F0.wireOp",EDGE,"E81.MirrorCS"),sQuery(id+"F0.wireOp",EDGE,"E132.trimOffspring")])]});
            var Q91;
            Q91=makeQuery(id+"F1.opExtrude","SWEPT_EDGE",EDGE,{"disambiguationData":[OSD([sQuery(id+"F0.wireOp",EDGE,"E71.MirrorCS"),sQuery(id+"F0.wireOp",EDGE,"E81.MirrorCS")])]});
            var Q92;
            Q92=makeQuery(id+"F1.opExtrude","SWEPT_EDGE",EDGE,{"disambiguationData":[OSD([sQuery(id+"F0.wireOp",EDGE,"E56.MirrorCS"),sQuery(id+"F0.wireOp",EDGE,"E123.trimOffspring")])]});
            var Q93;
            Q93=makeQuery(id+"F1.opExtrude","SWEPT_EDGE",EDGE,{"disambiguationData":[OSD([sQuery(id+"F0.wireOp",EDGE,"E56.MirrorCS"),sQuery(id+"F0.wireOp",EDGE,"E124.trimOffspring")])]});
            var Q94;
            Q94=makeQuery(id+"F1.opExtrude","SWEPT_EDGE",EDGE,{"disambiguationData":[OSD([sQuery(id+"F0.wireOp",EDGE,"E48.MirrorCS"),sQuery(id+"F0.wireOp",EDGE,"E121.trimOffspring")])]});
            var Q95;
            Q95=makeQuery(id+"F1.opExtrude","SWEPT_EDGE",EDGE,{"disambiguationData":[OSD([sQuery(id+"F0.wireOp",EDGE,"E49.MirrorCS"),sQuery(id+"F0.wireOp",EDGE,"E122.trimOffspring")])]});
            var Q96;
            Q96=makeQuery(id+"F1.opExtrude","SWEPT_EDGE",EDGE,{"disambiguationData":[OSD([sQuery(id+"F0.wireOp",EDGE,"E49.MirrorCS"),sQuery(id+"F0.wireOp",EDGE,"E121.trimOffspring")])]});
            var Q97;
            Q97=makeQuery(id+"F1.opExtrude","SWEPT_EDGE",EDGE,{"disambiguationData":[OSD([sQuery(id+"F0.wireOp",EDGE,"E64.MirrorCS"),sQuery(id+"F0.wireOp",EDGE,"E113.trimOffspring")])]});
            var Q98;
            Q98=makeQuery(id+"F1.opExtrude","SWEPT_EDGE",EDGE,{"disambiguationData":[OSD([sQuery(id+"F0.wireOp",EDGE,"E76.MirrorCS"),sQuery(id+"F0.wireOp",EDGE,"E85.MirrorCS")])]});
            var Q99;
            Q99=makeQuery(id+"F1.opExtrude","SWEPT_EDGE",EDGE,{"disambiguationData":[OSD([sQuery(id+"F0.wireOp",EDGE,"E85.MirrorCS"),sQuery(id+"F0.wireOp",EDGE,"E134.trimOffspring")])]});
            var Q100;
            Q100=makeQuery(id+"F1.opExtrude","SWEPT_EDGE",EDGE,{"disambiguationData":[OSD([sQuery(id+"F0.wireOp",EDGE,"E82.MirrorCS"),sQuery(id+"F0.wireOp",EDGE,"E113.trimOffspring")])]});
            var Q101;
            Q101=makeQuery(id+"F1.opExtrude","SWEPT_EDGE",EDGE,{"disambiguationData":[OSD([sQuery(id+"F0.wireOp",EDGE,"E86.MirrorCS"),sQuery(id+"F0.wireOp",EDGE,"E134.trimOffspring")])]});
            var Q102;
            Q102=makeQuery(id+"F1.opExtrude","SWEPT_EDGE",EDGE,{"disambiguationData":[OSD([sQuery(id+"F0.wireOp",EDGE,"E82.MirrorCS"),sQuery(id+"F0.wireOp",EDGE,"E114.trimOffspring")])]});
            var Q103;
            Q103=makeQuery(id+"F1.opExtrude","SWEPT_EDGE",EDGE,{"disambiguationData":[OSD([sQuery(id+"F0.wireOp",EDGE,"E76.MirrorCS"),sQuery(id+"F0.wireOp",EDGE,"E86.MirrorCS")])]});
            var Q104;
            Q104=makeQuery(id+"F1.opExtrude","SWEPT_EDGE",EDGE,{"disambiguationData":[OSD([sQuery(id+"F0.wireOp",EDGE,"E64.MirrorCS"),sQuery(id+"F0.wireOp",EDGE,"E114.trimOffspring")])]});
            var Q105;
            Q105=makeQuery(id+"F1.opExtrude","SWEPT_EDGE",EDGE,{"disambiguationData":[OSD([sQuery(id+"F0.wireOp",EDGE,"E9.trimOffspring"),sQuery(id+"F0.wireOp",EDGE,"E102.trimOffspring")])]});
            fillet(context, id + "F2", {"entities" : qUnion([Q0, Q1, Q2, Q3, Q4, Q5, Q6, Q7, Q8, Q9, Q10, Q11, Q12, Q13, Q14, Q15, Q16, Q17, Q18, Q19, Q20, Q21, Q22, Q23, Q24, Q25, Q26, Q27, Q28, Q29, Q30, Q31, Q32, Q33, Q34, Q35, Q36, Q37, Q38, Q39, Q40, Q41, Q42, Q43, Q44, Q45, Q46, Q47, Q48, Q49, Q50, Q51, Q52, Q53, Q54, Q55, Q56, Q57, Q58, Q59, Q60, Q61, Q62, Q63, Q64, Q65, Q66, Q67, Q68, Q69, Q70, Q71, Q72, Q73, Q74, Q75, Q76, Q77, Q78, Q79, Q80, Q81, Q82, Q83, Q84, Q85, Q86, Q87, Q88, Q89, Q90, Q91, Q92, Q93, Q94, Q95, Q96, Q97, Q98, Q99, Q100, Q101, Q102, Q103, Q104, Q105]), "radius" : 1 * mm, "tangentPropagation" : true, "allowEdgeOverflow" : false});
        }
    });
